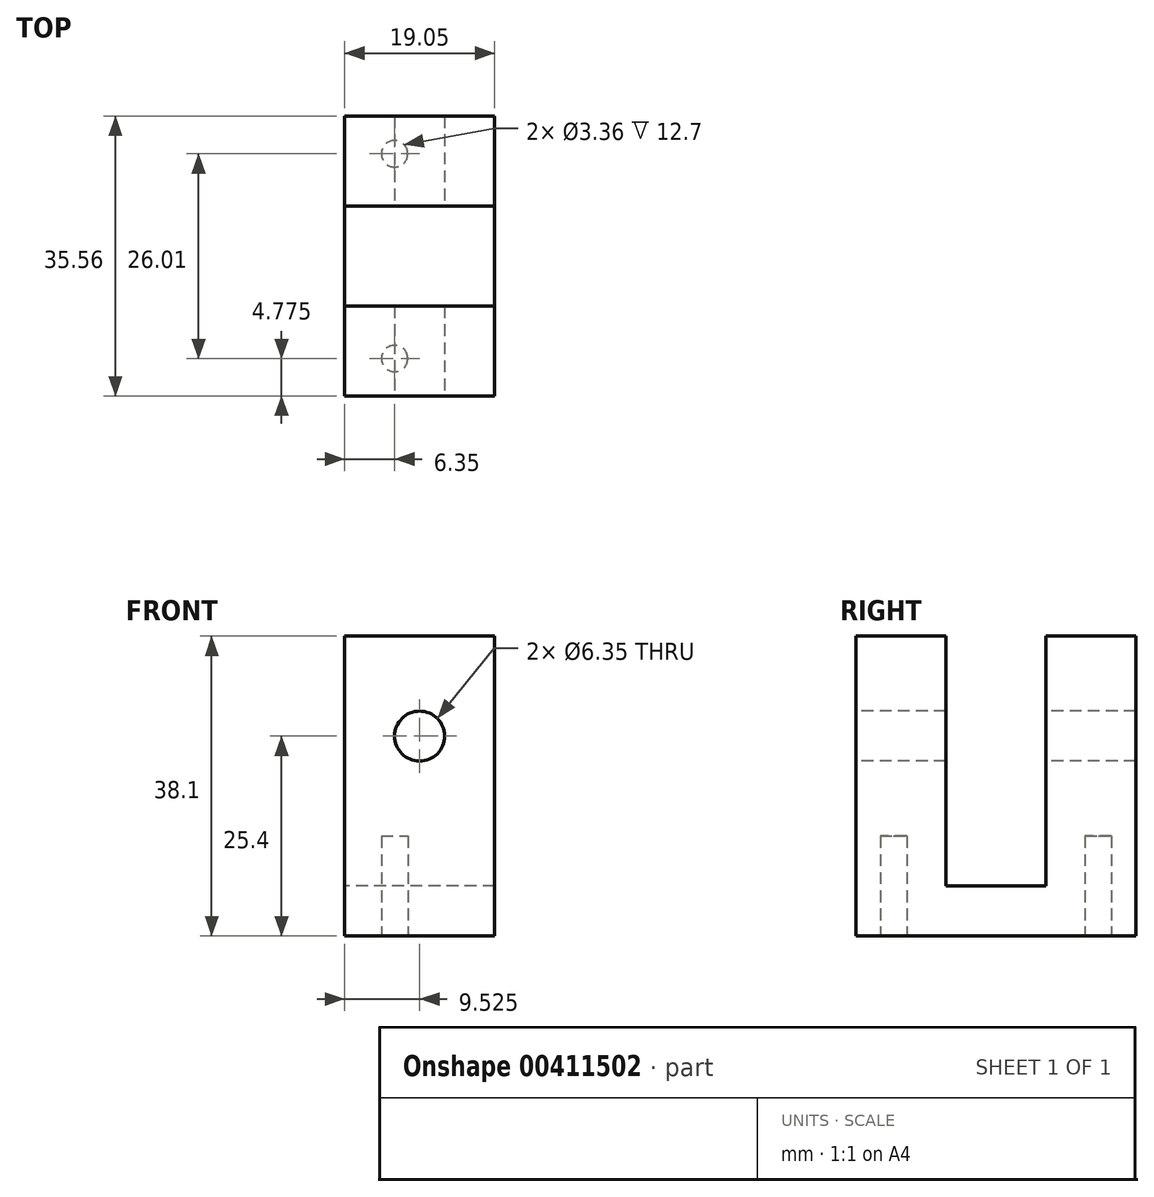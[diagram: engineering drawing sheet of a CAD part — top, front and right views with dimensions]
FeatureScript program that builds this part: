
annotation { "Feature Type Name" : "Feature", "Feature Type Description" : "" }
export const myFeature = defineFeature(function(context is Context, id is Id, definition is map)
    precondition{}
    {
        {
            var Q0;
            Q0=qCreatedBy(makeId("Right.planeOp"),FACE);
            var sketch = newSketch(context, id + "F0", { "sketchPlane" : qUnion([Q0])});
            skLineSegment(sketch, "E0", {"start": v(0, 38.1) * mm, "end": v(0, 0) * mm});
            skLineSegment(sketch, "E1", {"start": v(0, 0) * mm, "end": v(35.56, 0) * mm});
            skLineSegment(sketch, "E2", {"start": v(35.56, 0) * mm, "end": v(35.56, 38.1) * mm});
            skLineSegment(sketch, "E3", {"start": v(35.56, 38.1) * mm, "end": v(24.13, 38.1) * mm});
            skLineSegment(sketch, "E4", {"start": v(24.13, 38.1) * mm, "end": v(24.13, 6.35) * mm});
            skLineSegment(sketch, "E5", {"start": v(24.13, 6.35) * mm, "end": v(11.43, 6.35) * mm});
            skLineSegment(sketch, "E6", {"start": v(11.43, 6.35) * mm, "end": v(11.43, 38.1) * mm});
            skLineSegment(sketch, "E7", {"start": v(11.43, 38.1) * mm, "end": v(0, 38.1) * mm});
            skSolve(sketch);
        }
        {
            var Q0;
            Q0 = qSketchRegion(id + "F0", true);
            extrude(context, id + "F1", {"entities" : qUnion([Q0]), "depth" : 19.05 * mm});
        }
        {
            var Q0;
            Q0=makeQuery(id+"F1.opExtrude","SWEPT_FACE",FACE,{"disambiguationData":[OSD([sQuery(id+"F0.wireOp",EDGE,"E0")])]});
            var sketch = newSketch(context, id + "F2", { "sketchPlane" : qUnion([Q0])});
            skCircle(sketch, "E8", {"center": v(9.53, 25.4) * mm, "radius": 3.18 * mm});
            skPoint(sketch, "E8.centerSnap0", {"position": v(9.53, 38.1) * mm});
            skSolve(sketch);
        }
        {
            var Q0;
            Q0 = qSketchRegion(id + "F2", true);
            extrude(context, id + "F3", {"entities" : qUnion([Q0]), "operationType" : NewBodyOperationType.REMOVE, "oppositeDirection" : true, "depth" : 76.2 * mm});
        }
        {
            var Q0;
            Q0=makeQuery(id+"F1.opExtrude","SWEPT_FACE",FACE,{"disambiguationData":[OSD([sQuery(id+"F0.wireOp",EDGE,"E1")])]});
            var sketch = newSketch(context, id + "F4", { "sketchPlane" : qUnion([Q0])});
            skCircle(sketch, "E9", {"center": v(6.35, -4.78) * mm, "radius": 1.68 * mm});
            skCircle(sketch, "E10", {"center": v(6.35, -30.78) * mm, "radius": 1.68 * mm});
            skSolve(sketch);
        }
        {
            var Q0;
            Q0 = qSketchRegion(id + "F4", true);
            extrude(context, id + "F5", {"entities" : qUnion([Q0]), "operationType" : NewBodyOperationType.REMOVE, "oppositeDirection" : true, "depth" : 12.7 * mm});
        }
    });
